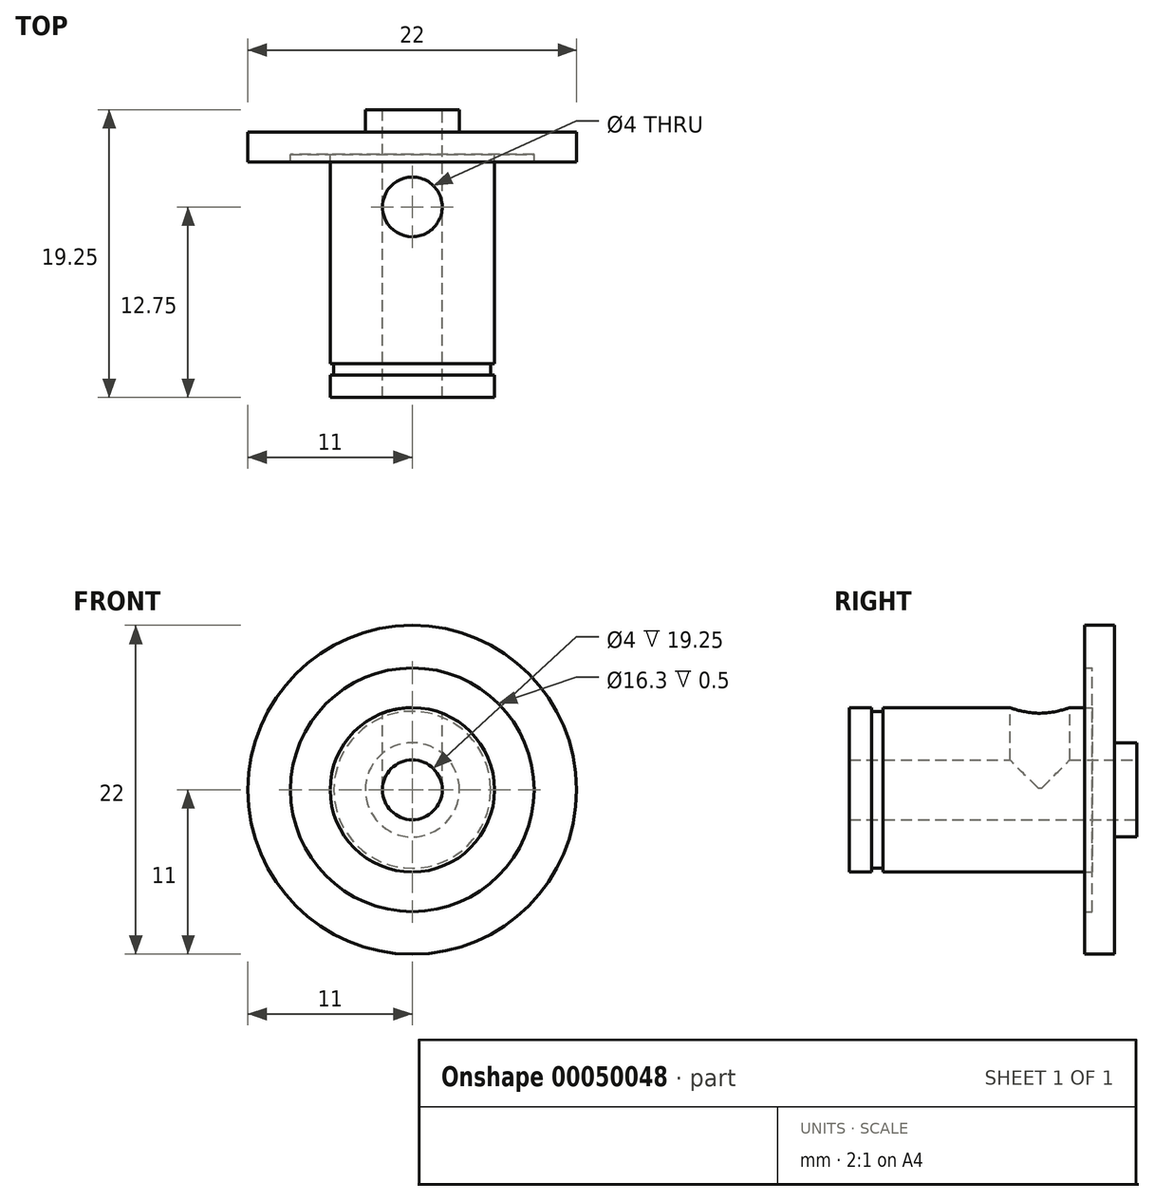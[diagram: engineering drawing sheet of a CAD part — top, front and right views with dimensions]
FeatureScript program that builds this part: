
annotation { "Feature Type Name" : "Feature", "Feature Type Description" : "" }
export const myFeature = defineFeature(function(context is Context, id is Id, definition is map)
    precondition{}
    {
        {
            var Q0;
            Q0=qCreatedBy(makeId("Front.planeOp"),FACE);
            var sketch = newSketch(context, id + "F0", { "sketchPlane" : qUnion([Q0])});
            skCircle(sketch, "E0", {"center": v(0, 0) * mm, "radius": 2 * mm});
            skCircle(sketch, "E1", {"center": v(0, 0) * mm, "radius": 3.15 * mm});
            skCircle(sketch, "E2", {"center": v(0, 0) * mm, "radius": 5.5 * mm});
            skCircle(sketch, "E3", {"center": v(0, 0) * mm, "radius": 11 * mm});
            skSolve(sketch);
        }
        {
            var Q0;
            Q0=qSketchRegion(id+"F0",true);
            var Q1;
            Q1=makeQuery(id+"F0.imprint","IMPRINT",FACE,{"disambiguationData":[TD([[makeQuery(id+"F0.imprint","IMPRINT",EDGE,{"derivedFrom":sQuery(id+"F0.wireOp",EDGE,"E1")}),-1.0]])]});
            var Q2;
            Q2=makeQuery(id+"F0.imprint","IMPRINT",FACE,{"disambiguationData":[TD([[makeQuery(id+"F0.imprint","IMPRINT",EDGE,{"derivedFrom":sQuery(id+"F0.wireOp",EDGE,"E0")}),-1.0]])]});
            extrude(context, id + "F1", {"entities" : qUnion([Q0, Q1, Q2]), "depth" : 1.5 * mm});
        }
        {
            var Q0;
            Q0=makeQuery(id+"F0.imprint","IMPRINT",FACE,{"disambiguationData":[TD([[makeQuery(id+"F0.imprint","IMPRINT",EDGE,{"derivedFrom":sQuery(id+"F0.wireOp",EDGE,"E1")}),-1.0]])]});
            var Q1;
            Q1=makeQuery(id+"F0.imprint","IMPRINT",FACE,{"disambiguationData":[TD([[makeQuery(id+"F0.imprint","IMPRINT",EDGE,{"derivedFrom":sQuery(id+"F0.wireOp",EDGE,"E0")}),-1.0]])]});
            extrude(context, id + "F2", {"entities" : qUnion([Q0, Q1]), "operationType" : NewBodyOperationType.ADD, "depth" : 17.75 * mm});
        }
        {
            var Q0;
            Q0=makeQuery(id+"F0.imprint","IMPRINT",FACE,{"disambiguationData":[TD([[makeQuery(id+"F0.imprint","IMPRINT",EDGE,{"derivedFrom":sQuery(id+"F0.wireOp",EDGE,"E0")}),-1.0]])]});
            extrude(context, id + "F3", {"entities" : qUnion([Q0]), "operationType" : NewBodyOperationType.ADD, "oppositeDirection" : true, "depth" : 1.5 * mm});
        }
        {
            var Q0;
            Q0=qCreatedBy(makeId("Right.planeOp"),FACE);
            var sketch = newSketch(context, id + "F4", { "sketchPlane" : qUnion([Q0])});
            skLineSegment(sketch, "E4", {"start": v(-20.03, 0) * mm, "end": v(3.26, 0) * mm, "construction": true});
            skLineSegment(sketch, "E5.bottom", {"start": v(-15.5, 5.5) * mm, "end": v(-16.25, 5.5) * mm});
            skLineSegment(sketch, "E5.top", {"start": v(-15.5, 5.25) * mm, "end": v(-16.25, 5.25) * mm});
            skLineSegment(sketch, "E5.left", {"start": v(-15.5, 5.5) * mm, "end": v(-15.5, 5.25) * mm});
            skLineSegment(sketch, "E5.right", {"start": v(-16.25, 5.5) * mm, "end": v(-16.25, 5.25) * mm});
            skSolve(sketch);
        }
        {
            var Q0;
            Q0=qSketchRegion(id+"F4",true);
            var Q1;
            Q1=sQuery(id+"F4.wireOp",EDGE,"E4");
            revolve(context, id + "F5", {"operationType" : NewBodyOperationType.REMOVE, "entities" : qUnion([Q0]), "axis" : qUnion([Q1]), "revolveType" : RevolveType.FULL, "oppositeDirection" : true});
        }
        {
            var Q0;
            Q0=qCreatedBy(makeId("Top.planeOp"),FACE);
            cPlane(context, id + "F6", {"entities" : qUnion([Q0]), "cplaneType" : CPlaneType.OFFSET, "offset" : 5.5 * mm, "width" : 150 * mm, "height" : 150 * mm});
        }
        {
            var Q0;
            Q0=qCreatedBy(id+"F6.planeOp",FACE);
            var sketch = newSketch(context, id + "F7", { "sketchPlane" : qUnion([Q0])});
            skPoint(sketch, "E6", {"position": v(0, -5) * mm});
            skLineSegment(sketch, "E7", {"start": v(0, 0) * mm, "end": v(0, -5) * mm});
            skSolve(sketch);
        }
        {
            var Q0;
            Q0=sQuery(id+"F7.wireOp",VERTEX,"E6");
            var Q1;
            Q1=makeQuery(id+"F1.opExtrude","SWEPT_BODY",BODY,{"disambiguationData":[OSD([sQuery(id+"F0.wireOp",EDGE,"E0"),sQuery(id+"F0.wireOp",EDGE,"E3")])]});
            hole(context, id + "F8", {"style" : HoleStyle.SIMPLE, "holeDiameter" : 4 * mm, "endStyle" : HoleEndStyle.BLIND, "holeDepth" : 5 * mm, "locations" : qUnion([Q0]), "scope" : qUnion([Q1])});
        }
        {
            var Q0;
            Q0=qCreatedBy(makeId("Front.planeOp"),FACE);
            var sketch = newSketch(context, id + "F9", { "sketchPlane" : qUnion([Q0])});
            skCircle(sketch, "E8", {"center": v(0, 0) * mm, "radius": 5.5 * mm});
            skCircle(sketch, "E9", {"center": v(0, 0) * mm, "radius": 8.15 * mm});
            skCircle(sketch, "E10", {"center": v(0, 0) * mm, "radius": 11 * mm});
            skSolve(sketch);
        }
        {
            var Q0;
            Q0=qSketchRegion(id+"F9",true);
            extrude(context, id + "F10", {"entities" : qUnion([Q0]), "depth" : 2 * mm});
        }
        {
            var Q0;
            Q0=makeQuery(id+"F9.imprint","IMPRINT",FACE,{"disambiguationData":[TD([[makeQuery(id+"F9.imprint","IMPRINT",EDGE,{"derivedFrom":sQuery(id+"F9.wireOp",EDGE,"E8")}),-1.0]])]});
            extrude(context, id + "F11", {"entities" : qUnion([Q0]), "operationType" : NewBodyOperationType.ADD, "depth" : .75 * mm});
        }
    });
